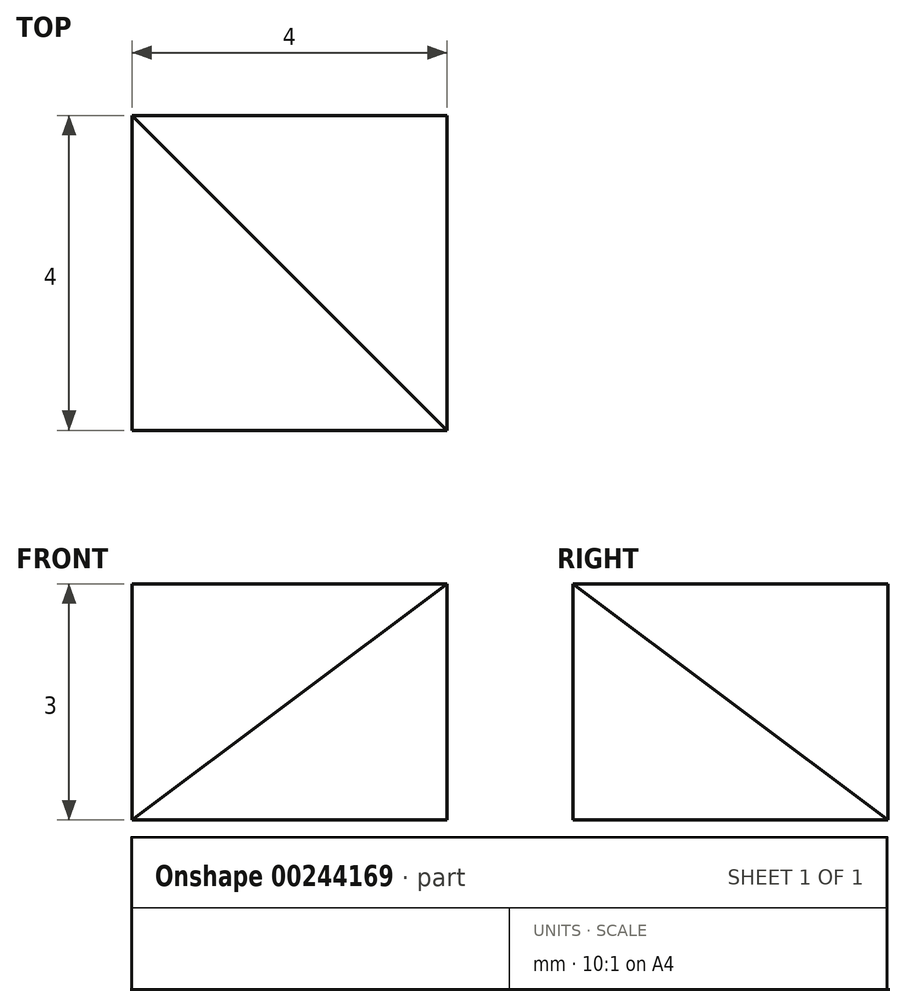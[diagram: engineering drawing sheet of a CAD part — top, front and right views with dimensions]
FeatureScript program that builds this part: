
annotation { "Feature Type Name" : "Feature", "Feature Type Description" : "" }
export const myFeature = defineFeature(function(context is Context, id is Id, definition is map)
    precondition{}
    {
        {
            var Q0;
            Q0=qCreatedBy(makeId("Top.planeOp"),FACE);
            var sketch = newSketch(context, id + "F0", { "sketchPlane" : qUnion([Q0])});
            skLineSegment(sketch, "E0.bottom", {"start": v(0, 0) * mm, "end": v(4, 0) * mm});
            skLineSegment(sketch, "E0.top", {"start": v(0, 4) * mm, "end": v(4, 4) * mm});
            skLineSegment(sketch, "E0.left", {"start": v(0, 0) * mm, "end": v(0, 4) * mm});
            skLineSegment(sketch, "E0.right", {"start": v(4, 0) * mm, "end": v(4, 4) * mm});
            skSolve(sketch);
        }
        {
            var Q0;
            Q0 = qSketchRegion(id + "F0", true);
            extrude(context, id + "F1", {"entities" : qUnion([Q0]), "depth" : 3 * mm});
        }
        {
            var Q0;
            Q0=qCreatedBy(makeId("Origin.pointOp"),VERTEX);
            var Q1;
            Q1=makeQuery(id+"F1.opExtrude","CAP_VERTEX",VERTEX,{"disambiguationData":[OSD([sQuery(id+"F0.wireOp",EDGE,"E0.top"),sQuery(id+"F0.wireOp",EDGE,"E0.left")])],"isStart":false});
            var Q2;
            Q2=makeQuery(id+"F1.opExtrude","CAP_VERTEX",VERTEX,{"disambiguationData":[OSD([sQuery(id+"F0.wireOp",EDGE,"E0.bottom"),sQuery(id+"F0.wireOp",EDGE,"E0.right")])],"isStart":false});
            cPlane(context, id + "F2", {"entities" : qUnion([Q0, Q1, Q2]), "cplaneType" : CPlaneType.THREE_POINT, "offset" : 25 * mm, "width" : 150 * mm, "height" : 150 * mm});
        }
        {
            var Q0;
            Q0=qCreatedBy(id+"F2.planeOp",FACE);
            var sketch = newSketch(context, id + "F3", { "sketchPlane" : qUnion([Q0])});
            skPoint(sketch, "E1.0", {"position": v(0, 0) * mm});
            skPoint(sketch, "E1.1", {"position": v(4.66, 1.8) * mm});
            skPoint(sketch, "E1.2", {"position": v(0, 5) * mm});
            skLineSegment(sketch, "E2", {"start": v(0, 0) * mm, "end": v(4.66, 1.8) * mm});
            skLineSegment(sketch, "E3", {"start": v(0, 5) * mm, "end": v(4.66, 1.8) * mm});
            skLineSegment(sketch, "E4", {"start": v(0, 5) * mm, "end": v(0, 0) * mm});
            skSolve(sketch);
        }
        {
            var Q0;
            Q0 = qSketchRegion(id + "F3", true);
            extrude(context, id + "F4", {"entities" : qUnion([Q0]), "operationType" : NewBodyOperationType.REMOVE, "depth" : 25 * mm});
        }
        {
            var Q0;
            Q0=makeQuery(id+"F4.boolean.opBoolean","MERGE",VERTEX,{"derivedFrom":[makeQuery(id+"F1.opExtrude","CAP_VERTEX",VERTEX,{"disambiguationData":[OSD([sQuery(id+"F0.wireOp",EDGE,"E0.bottom"),sQuery(id+"F0.wireOp",EDGE,"E0.right")])],"isStart":false}),makeQuery(id+"F4.opExtrude","CAP_VERTEX",VERTEX,{"disambiguationData":[OSD([sQuery(id+"F3.wireOp",EDGE,"E2"),sQuery(id+"F3.wireOp",EDGE,"E3")])],"isStart":true})]});
            var Q1;
            Q1=makeQuery(id+"F1.opExtrude","CAP_VERTEX",VERTEX,{"disambiguationData":[OSD([sQuery(id+"F0.wireOp",EDGE,"E0.top"),sQuery(id+"F0.wireOp",EDGE,"E0.right")])],"isStart":true});
            var Q2;
            Q2=makeQuery(id+"F4.boolean.opBoolean","MERGE",VERTEX,{"derivedFrom":[makeQuery(id+"F1.opExtrude","CAP_VERTEX",VERTEX,{"disambiguationData":[OSD([sQuery(id+"F0.wireOp",EDGE,"E0.top"),sQuery(id+"F0.wireOp",EDGE,"E0.left")])],"isStart":false}),makeQuery(id+"F4.opExtrude","CAP_VERTEX",VERTEX,{"disambiguationData":[OSD([sQuery(id+"F3.wireOp",EDGE,"E3"),sQuery(id+"F3.wireOp",EDGE,"E4")])],"isStart":true})]});
            cPlane(context, id + "F5", {"entities" : qUnion([Q0, Q1, Q2]), "cplaneType" : CPlaneType.THREE_POINT, "offset" : 25 * mm, "width" : 150 * mm, "height" : 150 * mm});
        }
        {
            var Q0;
            Q0=qCreatedBy(id+"F5.planeOp",FACE);
            var sketch = newSketch(context, id + "F6", { "sketchPlane" : qUnion([Q0])});
            skPoint(sketch, "E5.0", {"position": v(2.2, 1.8) * mm});
            skPoint(sketch, "E5.1", {"position": v(2.2, -3.2) * mm});
            skPoint(sketch, "E5.2", {"position": v(-2.47, -1.4) * mm});
            skLineSegment(sketch, "E6", {"start": v(2.2, 1.8) * mm, "end": v(-2.47, -1.4) * mm});
            skLineSegment(sketch, "E7", {"start": v(-2.47, -1.4) * mm, "end": v(2.2, -3.2) * mm});
            skLineSegment(sketch, "E8", {"start": v(2.2, -3.2) * mm, "end": v(2.2, 1.8) * mm});
            skSolve(sketch);
        }
        {
            var Q0;
            Q0 = qSketchRegion(id + "F6", true);
            extrude(context, id + "F7", {"entities" : qUnion([Q0]), "operationType" : NewBodyOperationType.REMOVE, "oppositeDirection" : true, "depth" : 25 * mm});
        }
    });
